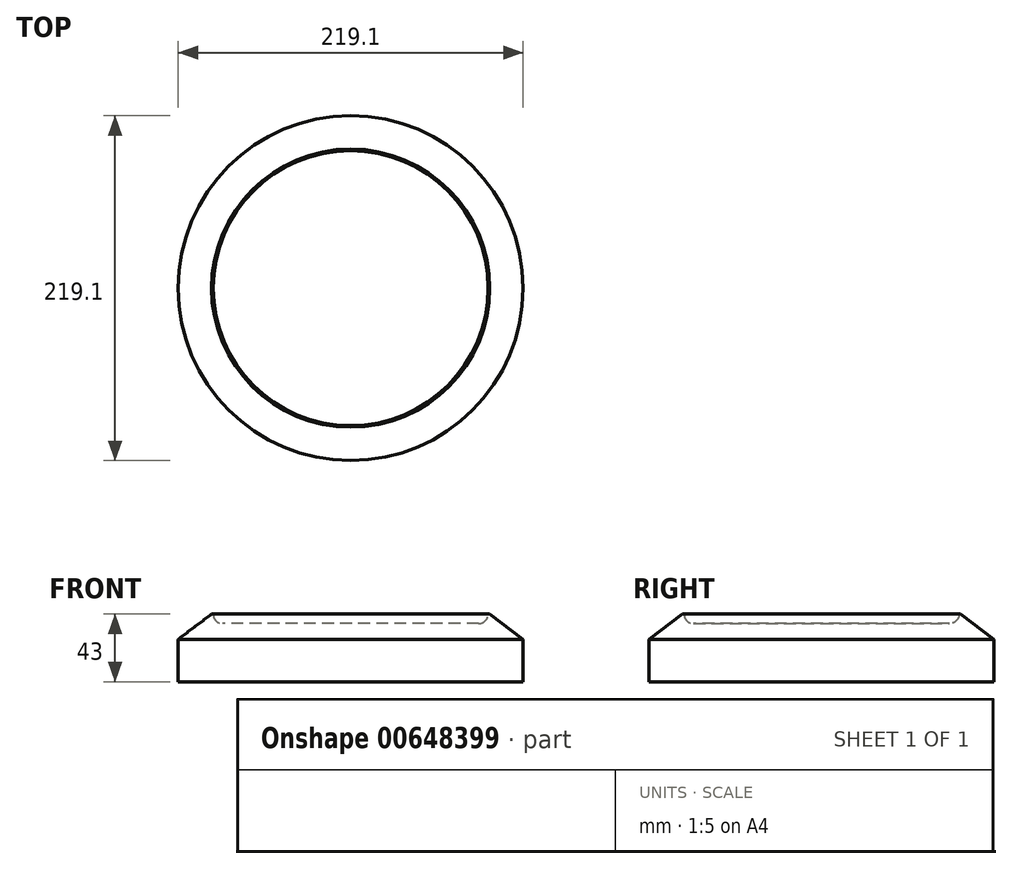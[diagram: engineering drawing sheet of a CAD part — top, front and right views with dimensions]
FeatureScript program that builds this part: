
annotation { "Feature Type Name" : "Feature", "Feature Type Description" : "" }
export const myFeature = defineFeature(function(context is Context, id is Id, definition is map)
    precondition{}
    {
        {
            var Q0;
            Q0=qCreatedBy(makeId("Front.planeOp"),FACE);
            var sketch = newSketch(context, id + "F0", { "sketchPlane" : qUnion([Q0])});
            skLineSegment(sketch, "E0", {"start": v(0, 0) * mm, "end": v(-109.55, 0) * mm});
            skLineSegment(sketch, "E1", {"start": v(-109.55, 0) * mm, "end": v(-109.55, 27) * mm});
            skLineSegment(sketch, "E2", {"start": v(-88.33, 43) * mm, "end": v(-87.33, 43) * mm});
            skLineSegment(sketch, "E3", {"start": v(-87.33, 43) * mm, "end": v(-87.33, 37) * mm});
            skLineSegment(sketch, "E4", {"start": v(-87.33, 37) * mm, "end": v(0, 37) * mm});
            skLineSegment(sketch, "E5", {"start": v(0, 0) * mm, "end": v(0, 37) * mm});
            skLineSegment(sketch, "E6", {"start": v(-87.33, 43) * mm, "end": v(-88.33, 43) * mm});
            skLineSegment(sketch, "E7", {"start": v(-88.33, 43) * mm, "end": v(-109.55, 27) * mm});
            skSolve(sketch);
        }
        {
            var Q0;
            Q0 = qSketchRegion(id + "F0", true);
            var Q1;
            Q1=sQuery(id+"F0.wireOp",EDGE,"E5");
            revolve(context, id + "F1", {"entities" : qUnion([Q0]), "axis" : qUnion([Q1]), "revolveType" : RevolveType.FULL});
        }
        {
            var Q0;
            Q0=makeQuery(id+"F1.opRevolve","SWEPT_EDGE",EDGE,{"disambiguationData":[OSD([sQuery(id+"F0.wireOp",EDGE,"E3"),sQuery(id+"F0.wireOp",EDGE,"E4")])]});
            fillet(context, id + "F2", {"entities" : qUnion([Q0]), "radius" : 6 * mm, "tangentPropagation" : true, "allowEdgeOverflow" : false});
        }
    });
